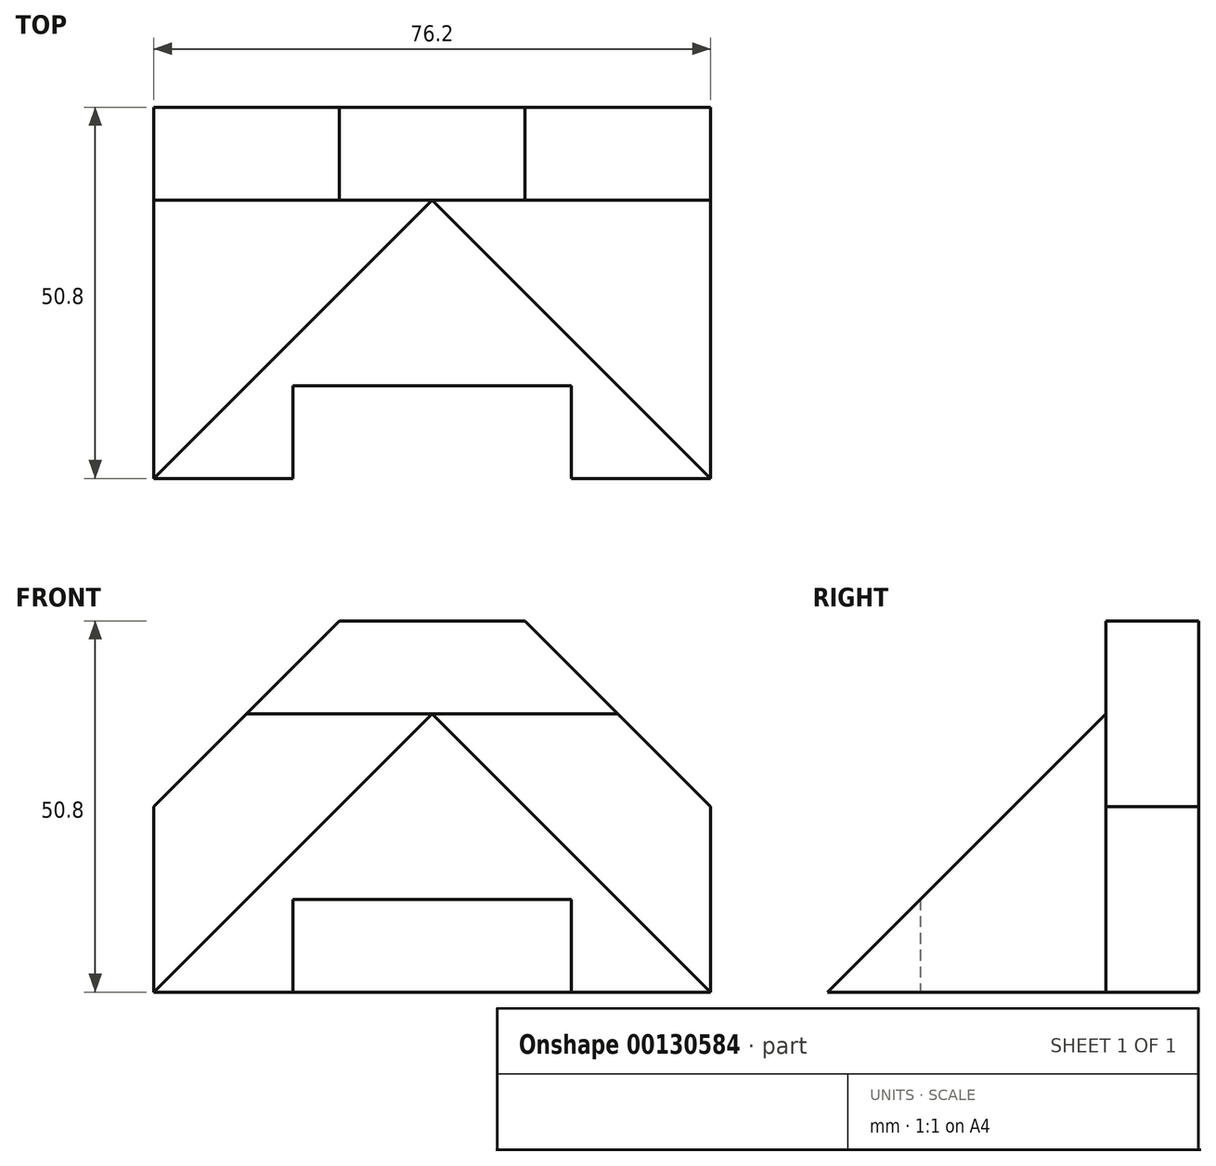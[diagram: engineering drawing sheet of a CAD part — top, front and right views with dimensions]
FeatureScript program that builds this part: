
annotation { "Feature Type Name" : "Feature", "Feature Type Description" : "" }
export const myFeature = defineFeature(function(context is Context, id is Id, definition is map)
    precondition{}
    {
        {
            var Q0;
            Q0=qCreatedBy(makeId("Front.planeOp"),FACE);
            var sketch = newSketch(context, id + "F0", { "sketchPlane" : qUnion([Q0])});
            skLineSegment(sketch, "E0", {"start": v(0, 0) * mm, "end": v(38.1, 0) * mm});
            skLineSegment(sketch, "E1", {"start": v(0, 0) * mm, "end": v(-38.1, 0) * mm});
            skLineSegment(sketch, "E2", {"start": v(-38.1, 0) * mm, "end": v(-38.1, 25.4) * mm});
            skLineSegment(sketch, "E3", {"start": v(-12.7, 50.8) * mm, "end": v(12.7, 50.8) * mm});
            skLineSegment(sketch, "E4", {"start": v(38.1, 25.4) * mm, "end": v(38.1, 0) * mm});
            skLineSegment(sketch, "E5", {"start": v(-38.1, 25.4) * mm, "end": v(-12.7, 50.8) * mm});
            skLineSegment(sketch, "E6", {"start": v(12.7, 50.8) * mm, "end": v(38.1, 25.4) * mm});
            skLineSegment(sketch, "E7", {"start": v(-38.1, 0) * mm, "end": v(0, 38.1) * mm});
            skLineSegment(sketch, "E8", {"start": v(0, 38.1) * mm, "end": v(38.1, 0) * mm});
            skLineSegment(sketch, "E9", {"start": v(19.05, 0) * mm, "end": v(19.05, 12.7) * mm});
            skLineSegment(sketch, "E10", {"start": v(19.05, 12.7) * mm, "end": v(-19.05, 12.7) * mm});
            skLineSegment(sketch, "E11", {"start": v(-19.05, 12.7) * mm, "end": v(-19.05, 0) * mm});
            skLineSegment(sketch, "E12", {"start": v(-19.05, 0) * mm, "end": v(-38.1, 0) * mm});
            skSolve(sketch);
        }
        {
            var Q0;
            Q0=makeQuery(id+"F0.imprint","IMPRINT",FACE,{"disambiguationData":[TD([[makeQuery(id+"F0.imprint","IMPRINT",EDGE,{"derivedFrom":sQuery(id+"F0.wireOp",EDGE,"E2")}),-1.0]])]});
            extrude(context, id + "F1", {"entities" : qUnion([Q0]), "depth" : 12.7 * mm});
        }
        {
            var Q0;
            Q0=makeQuery(id+"F0.imprint","IMPRINT",FACE,{"disambiguationData":[TD([[makeQuery(id+"F0.imprint","IMPRINT",EDGE,{"derivedFrom":sQuery(id+"F0.wireOp",EDGE,"E7")}),-1.0]])]});
            extrude(context, id + "F2", {"entities" : qUnion([Q0]), "operationType" : NewBodyOperationType.ADD, "depth" : 50.8 * mm});
        }
        {
            var Q0;
            Q0=qCreatedBy(makeId("Right.planeOp"),FACE);
            var sketch = newSketch(context, id + "F3", { "sketchPlane" : qUnion([Q0])});
            skLineSegment(sketch, "E13", {"start": v(-50.8, 0) * mm, "end": v(-12.7, 38.1) * mm});
            skLineSegment(sketch, "E14", {"start": v(-50.8, 0) * mm, "end": v(-50.8, 38.1) * mm});
            skLineSegment(sketch, "E15", {"start": v(-50.8, 38.1) * mm, "end": v(-12.7, 38.1) * mm});
            skSolve(sketch);
        }
        {
            var Q0;
            Q0 = qSketchRegion(id + "F3", true);
            extrude(context, id + "F4", {"entities" : qUnion([Q0]), "operationType" : NewBodyOperationType.REMOVE, "oppositeDirection" : true, "depth" : 50.8 * mm, "hasSecondDirection" : true, "secondDirectionOppositeDirection" : false, "secondDirectionDepth" : 50.8 * mm});
        }
        {
            var Q0;
            {var subQ1=sQuery(id+"F0.wireOp",EDGE,"E1");Q0=makeQuery(id+"F0.imprint","IMPRINT",FACE,{"disambiguationData":[TD([[makeQuery(id+"F0.imprint","IMPRINT",EDGE,{"derivedFrom":subQ1}),-1.0]])]});}
            extrude(context, id + "F5", {"entities" : qUnion([Q0]), "operationType" : NewBodyOperationType.ADD, "depth" : 38.1 * mm});
        }
    });
